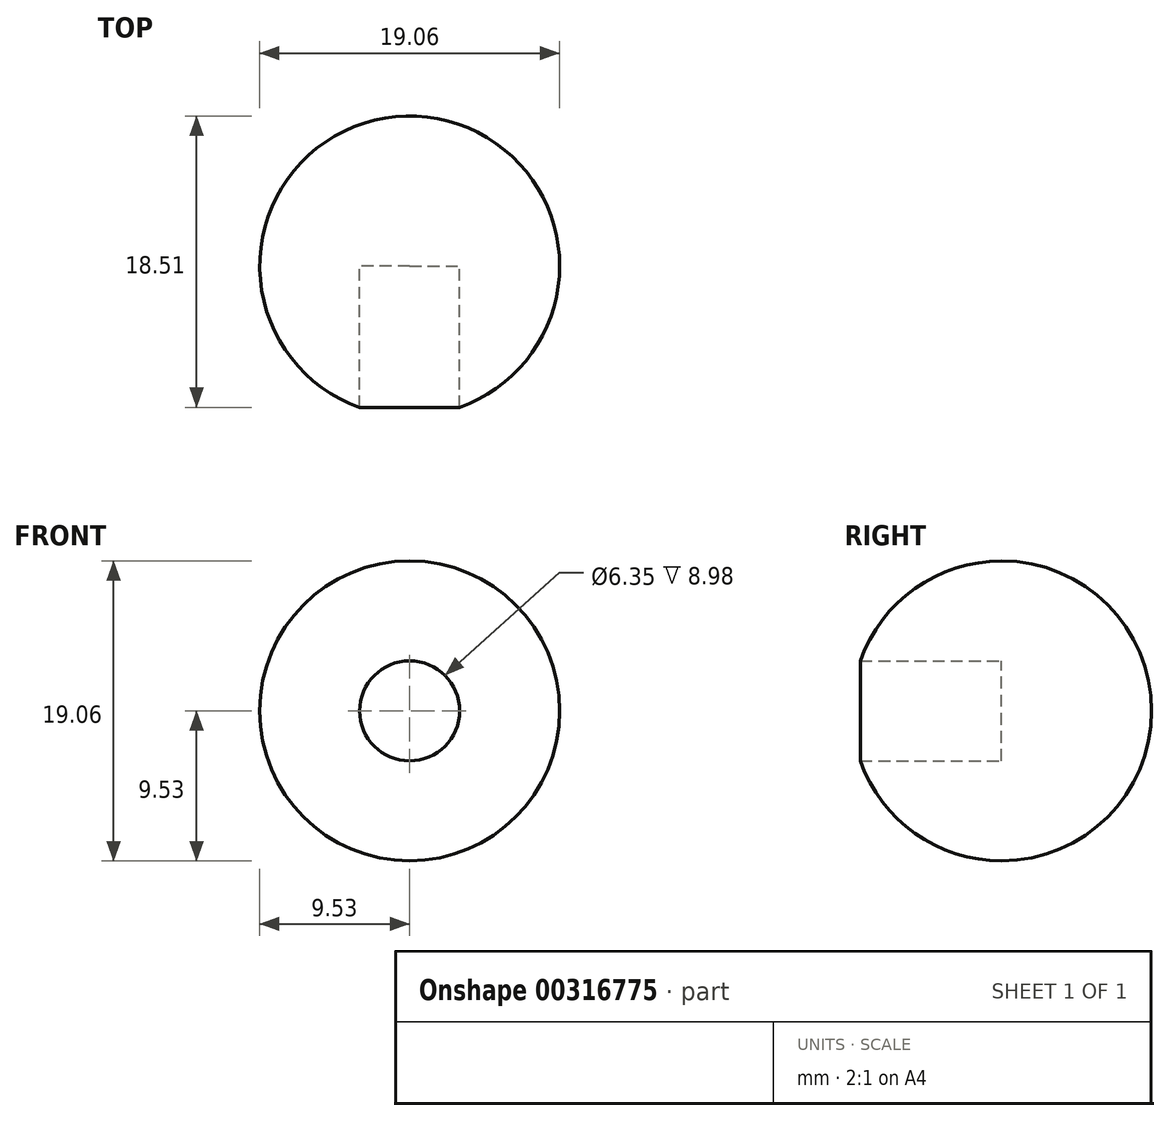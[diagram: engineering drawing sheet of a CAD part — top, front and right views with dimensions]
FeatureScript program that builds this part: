
annotation { "Feature Type Name" : "Feature", "Feature Type Description" : "" }
export const myFeature = defineFeature(function(context is Context, id is Id, definition is map)
    precondition{}
    {
        {
            var Q0;
            Q0=qCreatedBy(makeId("Front.planeOp"),FACE);
            var sketch = newSketch(context, id + "F0", { "sketchPlane" : qUnion([Q0])});
            skArc(sketch, "E0", {"start": v(0, 9.53) * mm, "mid": v(-9.53, 0) * mm, "end": v(0, -9.53) * mm});
            skLineSegment(sketch, "E1", {"start": v(0, 9.53) * mm, "end": v(0, -9.53) * mm});
            skSolve(sketch);
        }
        {
            var Q0;
            Q0=qCreatedBy(makeId("Top.planeOp"),FACE);
            var sketch = newSketch(context, id + "F1", { "sketchPlane" : qUnion([Q0])});
            skCircle(sketch, "E2", {"center": v(0, 0) * mm, "radius": 9.53 * mm});
            skSolve(sketch);
        }
        {
            var Q0;
            Q0=makeQuery(id+"F0.imprint","IMPRINT",FACE,{"disambiguationData":[TD([[makeQuery(id+"F0.imprint","IMPRINT",EDGE,{"derivedFrom":sQuery(id+"F0.wireOp",EDGE,"E0")}),1.0]])]});
            var Q1;
            Q1=sQuery(id+"F1.wireOp",EDGE,"E2");
            revolve(context, id + "F2", {"entities" : qUnion([Q0]), "axis" : qUnion([Q1]), "revolveType" : RevolveType.FULL});
        }
        {
            var Q0;
            Q0=qCreatedBy(makeId("Front.planeOp"),FACE);
            var sketch = newSketch(context, id + "F3", { "sketchPlane" : qUnion([Q0])});
            skCircle(sketch, "E3", {"center": v(0, 0) * mm, "radius": 3.18 * mm});
            skSolve(sketch);
        }
        {
            var Q0;
            Q0 = qSketchRegion(id + "F3", true);
            extrude(context, id + "F4", {"entities" : qUnion([Q0]), "depth" : 25.4 * mm});
        }
        {
            var Q0;
            Q0=makeQuery(id+"F4.opExtrude","SWEPT_BODY",BODY,{"disambiguationData":[OSD([sQuery(id+"F3.wireOp",EDGE,"E3")])]});
            var Q1;
            Q1=makeQuery(id+"F2.opRevolve","SWEPT_BODY",BODY,{"disambiguationData":[OSD([sQuery(id+"F0.wireOp",EDGE,"E0"),sQuery(id+"F0.wireOp",EDGE,"E1")])]});
            booleanBodies(context, id + "F5", {"operationType" : BooleanOperationType.SUBTRACTION, "tools" : qUnion([Q0]), "targets" : qUnion([Q1])});
        }
    });
